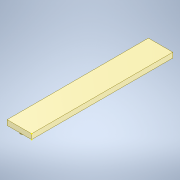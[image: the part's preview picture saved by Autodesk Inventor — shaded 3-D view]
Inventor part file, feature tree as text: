
AUTODESK INVENTOR PART (.ipt)
format: ipt  version: 2021 (Build 250183000, 183)  size: 126,464 bytes
history: native  units: mm
features: sketch x5, extrude x3, pattern_linear x1
ambient origin geometry x8: Origin, YZ Plane, XZ Plane, XY Plane, X Axis, Y Axis, Z Axis, Center Point
bodies: Solid1 (feature_tree)
feature tree (9):
  extrude  "Extrusion1"  Depth=140.0mm
  sketch  "Sketch2"  dims[d2=5.0mm d3=0.0mm d4=3.0mm]
  extrude  "Extrusion2"  Depth=5.0mm
  sketch  "Sketch4"  dims[d8=1.5mm d9=0.0mm d10=20.0mm d12=135.0mm]
  extrude  "Extrusion3"  Depth=1.0mm
  pattern_linear  "Rectangular Pattern1"  Count1=2 Spacing1=135.0mm
  sketch  "Sketch1"  dims[d0=24.226mm d1=140.0mm]
  sketch  "Sketch3"  dims[d5=2.0mm d6=0.0mm d7=1.0mm]
  sketch  "Sketch5"
